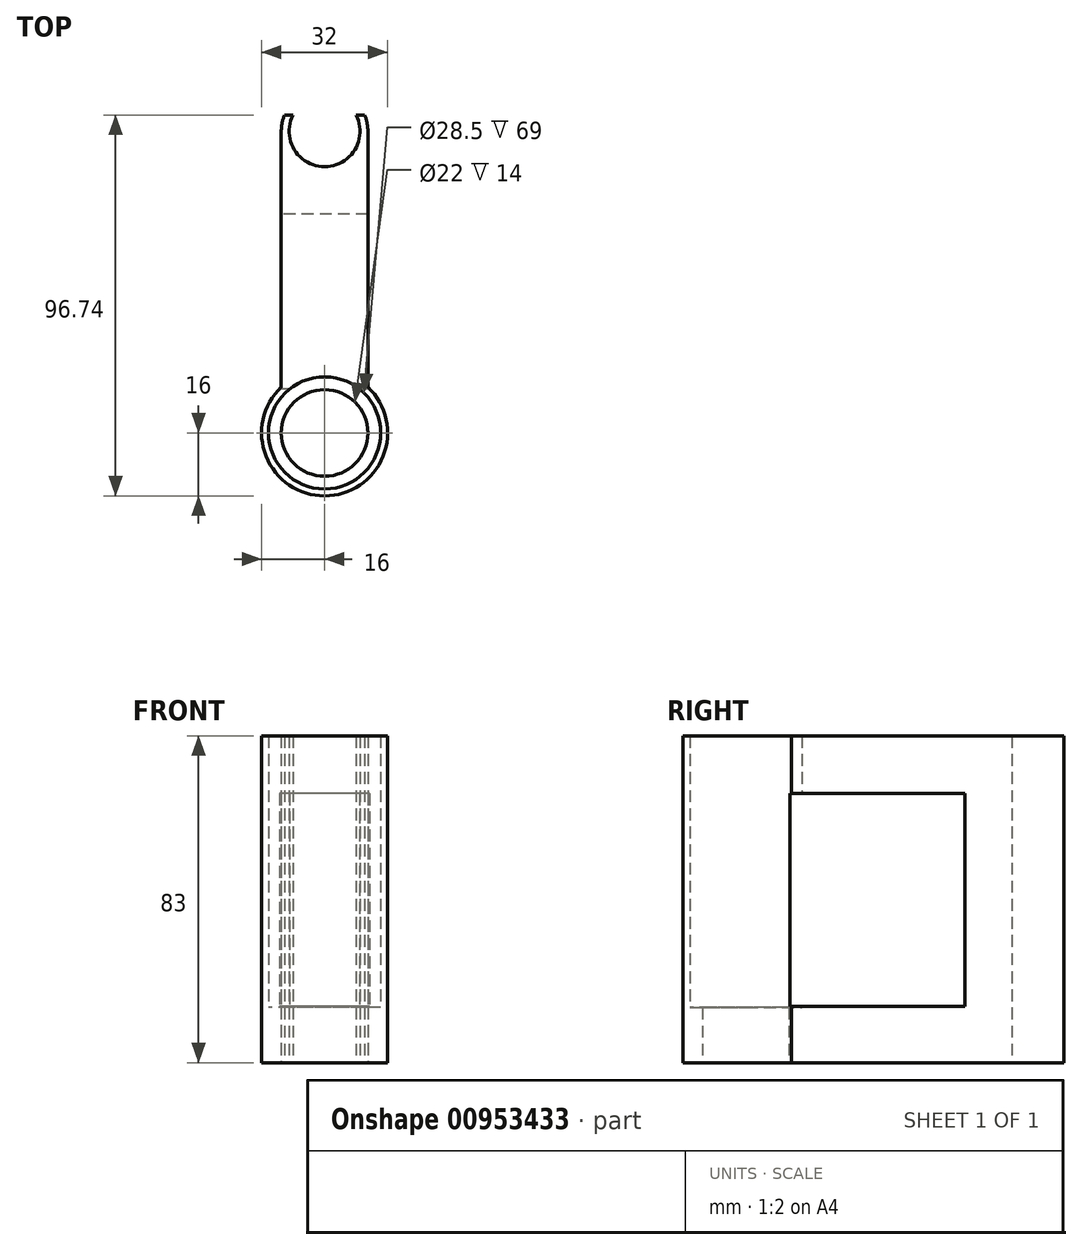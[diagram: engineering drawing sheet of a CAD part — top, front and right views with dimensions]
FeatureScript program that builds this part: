
annotation { "Feature Type Name" : "Feature", "Feature Type Description" : "" }
export const myFeature = defineFeature(function(context is Context, id is Id, definition is map)
    precondition{}
    {
        {
            var Q0;
            Q0=qCreatedBy(makeId("Top.planeOp"),FACE);
            var sketch = newSketch(context, id + "F0", { "sketchPlane" : qUnion([Q0])});
            skCircle(sketch, "E0", {"center": v(0, 0) * mm, "radius": 16 * mm});
            skArc(sketch, "E1", {"start": v(-10.2, 80.74) * mm, "mid": v(0, 65.62) * mm, "end": v(10.2, 80.74) * mm});
            skLineSegment(sketch, "E2", {"start": v(11, 76.62) * mm, "end": v(11, 11.62) * mm});
            skLineSegment(sketch, "E3", {"start": v(-11, 76.62) * mm, "end": v(-11, 11.62) * mm});
            skArc(sketch, "E4", {"start": v(-8, 80.74) * mm, "mid": v(0, 67.62) * mm, "end": v(8, 80.74) * mm});
            skLineSegment(sketch, "E5", {"start": v(-10.2, 80.74) * mm, "end": v(-8, 80.74) * mm});
            skLineSegment(sketch, "E6.trimOffspring", {"start": v(8, 80.74) * mm, "end": v(10.2, 80.74) * mm});
            skLineSegment(sketch, "E7", {"start": v(-10.2, 80.74) * mm, "end": v(10.2, 80.74) * mm});
            skCircle(sketch, "E8", {"center": v(0, 0) * mm, "radius": 14.25 * mm});
            skSolve(sketch);
        }
        {
            var Q0;
            Q0=makeQuery(id+"F0.imprint","IMPRINT",FACE,{"disambiguationData":[TD([[makeQuery(id+"F0.imprint","IMPRINT",EDGE,{"derivedFrom":sQuery(id+"F0.wireOp",EDGE,"E8")}),-1.0]])]});
            var Q1;
            Q1=makeQuery(id+"F0.imprint","IMPRINT",FACE,{"disambiguationData":[TD([[makeQuery(id+"F0.imprint","IMPRINT",EDGE,{"derivedFrom":sQuery(id+"F0.wireOp",EDGE,"E4")}),-1.0]])]});
            var Q2;
            {var subQ0=sQuery(id+"F0.wireOp",EDGE,"E2");Q2=makeQuery(id+"F0.imprint","IMPRINT",FACE,{"disambiguationData":[TD([[makeQuery(id+"F0.imprint","IMPRINT",EDGE,{"derivedFrom":subQ0}),-1.0]])]});}
            extrude(context, id + "F1", {"entities" : qUnion([Q0, Q1, Q2]), "depth" : 83 * mm, "offsetDistance" : 25 * mm});
        }
        {
            var Q0;
            Q0=qCreatedBy(makeId("Right.planeOp"),FACE);
            var sketch = newSketch(context, id + "F2", { "sketchPlane" : qUnion([Q0])});
            skLineSegment(sketch, "E9.bottom", {"start": v(11.18, 14.25) * mm, "end": v(55.65, 14.25) * mm});
            skLineSegment(sketch, "E9.top", {"start": v(11.18, 68.4) * mm, "end": v(55.65, 68.4) * mm});
            skLineSegment(sketch, "E9.left", {"start": v(11.18, 14.25) * mm, "end": v(11.18, 68.4) * mm});
            skLineSegment(sketch, "E9.right", {"start": v(55.65, 14.25) * mm, "end": v(55.65, 68.4) * mm});
            skSolve(sketch);
        }
        {
            var Q0;
            Q0=makeQuery(id+"F2.imprint","IMPRINT",FACE,{"disambiguationData":[TD([[makeQuery(id+"F2.imprint","IMPRINT",EDGE,{"derivedFrom":sQuery(id+"F2.wireOp",EDGE,"E9.bottom")}),1.0]])]});
            extrude(context, id + "F3", {"entities" : qUnion([Q0]), "operationType" : NewBodyOperationType.REMOVE, "endBound" : BoundingType.SYMMETRIC, "depth" : 25 * mm, "offsetDistance" : 25 * mm});
        }
        {
            var Q0;
            Q0=qCreatedBy(makeId("Top.planeOp"),FACE);
            var sketch = newSketch(context, id + "F4", { "sketchPlane" : qUnion([Q0])});
            skCircle(sketch, "E10", {"center": v(0, 0) * mm, "radius": 14.97 * mm});
            skCircle(sketch, "E11", {"center": v(0, 0) * mm, "radius": 11 * mm});
            skSolve(sketch);
        }
        {
            var Q0;
            Q0 = qSketchRegion(id + "F4", true);
            extrude(context, id + "F5", {"entities" : qUnion([Q0]), "operationType" : NewBodyOperationType.ADD, "depth" : 14 * mm, "offsetDistance" : 25 * mm});
        }
    });
